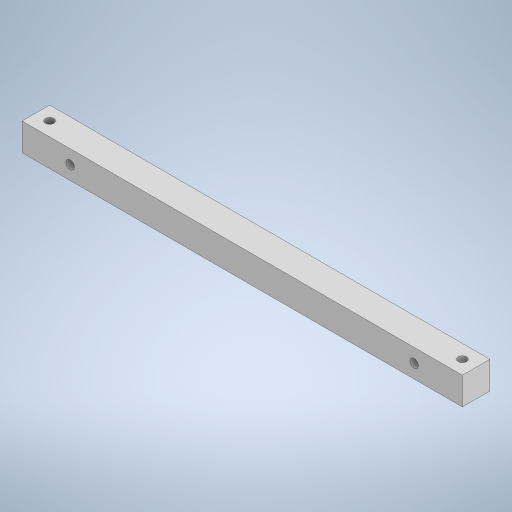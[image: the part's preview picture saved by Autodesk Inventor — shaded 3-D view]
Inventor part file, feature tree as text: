
AUTODESK INVENTOR PART (.ipt)
format: ipt  version: 2023 (Build 270158000, 158)  size: 242,176 bytes
history: native  units: mm
features: sketch x3, hole x2, other x1, extrude x1
ambient origin geometry x8: Origin, YZ Plane, XZ Plane, XY Plane, X Axis, Y Axis, Z Axis, Center Point
bodies: Body1 (feature_tree)
feature tree (7):
  other  "ソリッド1"
  extrude  "押し出し1"  Depth=160.0mm
  hole  "穴1"  [1 undecoded]
  hole  "穴2"  [1 undecoded]
  sketch  "スケッチ1"
  sketch  "スケッチ2"
  sketch  "スケッチ3"
note: 2 required parameter values undecoded (feature->parameter linkage not recoverable at this tier; creation-order binding heuristic only, values carry confidence <= 0.55)
